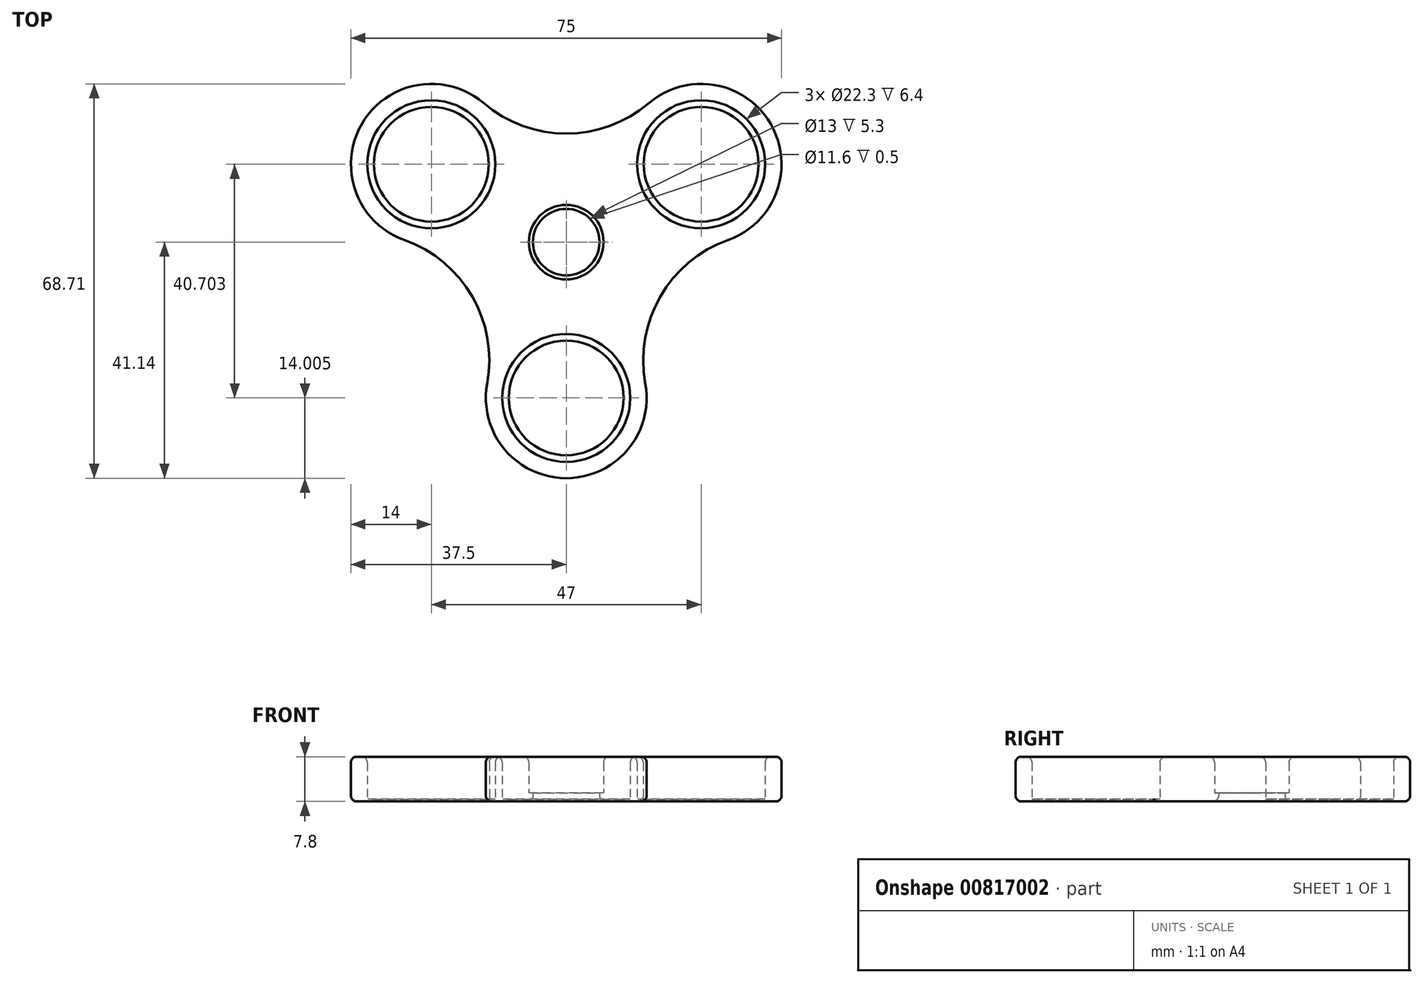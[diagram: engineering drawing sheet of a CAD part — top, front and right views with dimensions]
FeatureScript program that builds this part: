
annotation { "Feature Type Name" : "Feature", "Feature Type Description" : "" }
export const myFeature = defineFeature(function(context is Context, id is Id, definition is map)
    precondition{}
    {
        {
            var Q0;
            Q0=qCreatedBy(makeId("Top.planeOp"),FACE);
            var sketch = newSketch(context, id + "F0", { "sketchPlane" : qUnion([Q0])});
            skCircle(sketch, "E0.cCircle", {"center": v(0, 0) * mm, "radius": 13.57 * mm, "construction": true});
            skLineSegment(sketch, "E0.0", {"start": v(-23.5, 13.57) * mm, "end": v(23.5, 13.57) * mm, "construction": true});
            skLineSegment(sketch, "E0.1", {"start": v(23.5, 13.57) * mm, "end": v(0, -27.14) * mm, "construction": true});
            skLineSegment(sketch, "E0.2", {"start": v(0, -27.14) * mm, "end": v(-23.5, 13.57) * mm, "construction": true});
            skPoint(sketch, "E0.0.midPoint", {"position": v(0, 13.57) * mm});
            skCircle(sketch, "E1", {"center": v(-23.5, 13.57) * mm, "radius": 11.15 * mm});
            skCircle(sketch, "E2", {"center": v(-23.5, 13.57) * mm, "radius": 14 * mm});
            skCircle(sketch, "E3", {"center": v(0, -27.14) * mm, "radius": 11.15 * mm});
            skCircle(sketch, "E4", {"center": v(0, -27.14) * mm, "radius": 14 * mm});
            skCircle(sketch, "E5", {"center": v(23.5, 13.57) * mm, "radius": 14 * mm});
            skCircle(sketch, "E6", {"center": v(23.5, 13.57) * mm, "radius": 11.15 * mm});
            skCircle(sketch, "E7", {"center": v(0, 0) * mm, "radius": 41.14 * mm, "construction": true});
            skPoint(sketch, "E8", {"position": v(-11.75, -6.78) * mm});
            skPoint(sketch, "E9", {"position": v(11.75, -6.78) * mm});
            skLineSegment(sketch, "E10", {"start": v(0, 0) * mm, "end": v(-11.75, -6.78) * mm, "construction": true});
            skLineSegment(sketch, "E11", {"start": v(0, 0) * mm, "end": v(0, 13.57) * mm, "construction": true});
            skLineSegment(sketch, "E12", {"start": v(0, 0) * mm, "end": v(11.75, -6.78) * mm, "construction": true});
            skLineSegment(sketch, "E13", {"start": v(-11.75, -6.78) * mm, "end": v(-35.62, -20.57) * mm, "construction": true});
            skLineSegment(sketch, "E14", {"start": v(11.75, -6.78) * mm, "end": v(35.62, -20.57) * mm, "construction": true});
            skLineSegment(sketch, "E15", {"start": v(0, 13.57) * mm, "end": v(0, 41.14) * mm, "construction": true});
            skCircle(sketch, "E16", {"center": v(0, 41.14) * mm, "radius": 22.22 * mm});
            skCircle(sketch, "E17", {"center": v(-35.62, -20.57) * mm, "radius": 22.22 * mm});
            skCircle(sketch, "E18", {"center": v(35.62, -20.57) * mm, "radius": 22.22 * mm});
            skCircle(sketch, "E19", {"center": v(0, 0) * mm, "radius": 6.5 * mm});
            skSolve(sketch);
        }
        {
            var Q0;
            Q0=makeQuery(id+"F0.imprint","IMPRINT",FACE,{"disambiguationData":[TD([[makeQuery(id+"F0.imprint","IMPRINT",EDGE,{"derivedFrom":sQuery(id+"F0.wireOp",EDGE,"E19")}),-1.0]])]});
            var Q1;
            Q1=makeQuery(id+"F0.imprint","IMPRINT",FACE,{"disambiguationData":[TD([[makeQuery(id+"F0.imprint","IMPRINT",EDGE,{"derivedFrom":sQuery(id+"F0.wireOp",EDGE,"E1")}),-1.0]])]});
            var Q2;
            Q2=makeQuery(id+"F0.imprint","IMPRINT",FACE,{"disambiguationData":[TD([[makeQuery(id+"F0.imprint","IMPRINT",EDGE,{"derivedFrom":sQuery(id+"F0.wireOp",EDGE,"E6")}),-1.0]])]});
            var Q3;
            Q3=makeQuery(id+"F0.imprint","IMPRINT",FACE,{"disambiguationData":[TD([[makeQuery(id+"F0.imprint","IMPRINT",EDGE,{"derivedFrom":sQuery(id+"F0.wireOp",EDGE,"E3")}),-1.0]])]});
            extrude(context, id + "F1", {"entities" : qUnion([Q0, Q1, Q2, Q3]), "depth" : 7.8 * mm, "offsetDistance" : 25 * mm});
        }
        {
            var Q0;
            Q0=makeQuery(id+"F1.opExtrude","CAP_FACE",FACE,{"disambiguationData":[OSD([sQuery(id+"F0.wireOp",EDGE,"E1"),sQuery(id+"F0.wireOp",EDGE,"E2"),sQuery(id+"F0.wireOp",EDGE,"E3"),sQuery(id+"F0.wireOp",EDGE,"E4"),sQuery(id+"F0.wireOp",EDGE,"E5"),sQuery(id+"F0.wireOp",EDGE,"E6"),sQuery(id+"F0.wireOp",EDGE,"E16"),sQuery(id+"F0.wireOp",EDGE,"E17"),sQuery(id+"F0.wireOp",EDGE,"E18"),sQuery(id+"F0.wireOp",EDGE,"E19")])],"isStart":true});
            var sketch = newSketch(context, id + "F2", { "sketchPlane" : qUnion([Q0])});
            skCircle(sketch, "E20", {"center": v(0, 27.14) * mm, "radius": 10 * mm});
            skCircle(sketch, "E21", {"center": v(23.5, -13.57) * mm, "radius": 10 * mm});
            skCircle(sketch, "E22", {"center": v(-23.5, -13.57) * mm, "radius": 10 * mm});
            skCircle(sketch, "E23", {"center": v(0, 27.14) * mm, "radius": 11.15 * mm});
            skCircle(sketch, "E24", {"center": v(23.5, -13.57) * mm, "radius": 11.15 * mm});
            skCircle(sketch, "E25", {"center": v(-23.5, -13.57) * mm, "radius": 11.15 * mm});
            skSolve(sketch);
        }
        {
            var Q0;
            Q0 = qSketchRegion(id + "F2", true);
            extrude(context, id + "F3", {"entities" : qUnion([Q0]), "operationType" : NewBodyOperationType.ADD, "oppositeDirection" : true, "depth" : 0.4 * mm, "offsetDistance" : 25 * mm});
        }
        {
            var Q0;
            Q0=makeQuery(id+"F3.boolean.opBoolean","MERGE",FACE,{"derivedFrom":[makeQuery(id+"F1.opExtrude","CAP_FACE",FACE,{"disambiguationData":[OSD([sQuery(id+"F0.wireOp",EDGE,"E1"),sQuery(id+"F0.wireOp",EDGE,"E2"),sQuery(id+"F0.wireOp",EDGE,"E3"),sQuery(id+"F0.wireOp",EDGE,"E4"),sQuery(id+"F0.wireOp",EDGE,"E5"),sQuery(id+"F0.wireOp",EDGE,"E6"),sQuery(id+"F0.wireOp",EDGE,"E16"),sQuery(id+"F0.wireOp",EDGE,"E17"),sQuery(id+"F0.wireOp",EDGE,"E18"),sQuery(id+"F0.wireOp",EDGE,"E19")])],"isStart":true}),makeQuery(id+"F3.opExtrude","CAP_FACE",FACE,{"disambiguationData":[OSD([sQuery(id+"F2.wireOp",EDGE,"E20"),sQuery(id+"F2.wireOp",EDGE,"E23")])],"isStart":true}),makeQuery(id+"F3.opExtrude","CAP_FACE",FACE,{"disambiguationData":[OSD([sQuery(id+"F2.wireOp",EDGE,"E21"),sQuery(id+"F2.wireOp",EDGE,"E24")])],"isStart":true}),makeQuery(id+"F3.opExtrude","CAP_FACE",FACE,{"disambiguationData":[OSD([sQuery(id+"F2.wireOp",EDGE,"E22"),sQuery(id+"F2.wireOp",EDGE,"E25")])],"isStart":true})]});
            var sketch = newSketch(context, id + "F4", { "sketchPlane" : qUnion([Q0])});
            skCircle(sketch, "E26", {"center": v(0, 0) * mm, "radius": 5.8 * mm});
            skCircle(sketch, "E27", {"center": v(0, 0) * mm, "radius": 6.5 * mm});
            skSolve(sketch);
        }
        {
            var Q0;
            Q0 = qSketchRegion(id + "F4", true);
            extrude(context, id + "F5", {"entities" : qUnion([Q0]), "operationType" : NewBodyOperationType.ADD, "oppositeDirection" : true, "depth" : 1.5 * mm, "offsetDistance" : 25 * mm});
        }
        {
            var Q0;
            Q0=makeQuery(id+"F1.opExtrude","CAP_EDGE",EDGE,{"disambiguationData":[OSD([sQuery(id+"F0.wireOp",EDGE,"E1")])],"isStart":false});
            var Q1;
            Q1=makeQuery(id+"F1.opExtrude","CAP_EDGE",EDGE,{"disambiguationData":[OSD([sQuery(id+"F0.wireOp",EDGE,"E3")])],"isStart":false});
            var Q2;
            Q2=makeQuery(id+"F1.opExtrude","CAP_EDGE",EDGE,{"disambiguationData":[OSD([sQuery(id+"F0.wireOp",EDGE,"E19")])],"isStart":false});
            var Q3;
            Q3=makeQuery(id+"F1.opExtrude","CAP_EDGE",EDGE,{"disambiguationData":[OSD([sQuery(id+"F0.wireOp",EDGE,"E6")])],"isStart":false});
            var Q4;
            Q4=makeQuery(id+"F1.opExtrude","CAP_FACE",FACE,{"disambiguationData":[OSD([sQuery(id+"F0.wireOp",EDGE,"E1"),sQuery(id+"F0.wireOp",EDGE,"E2"),sQuery(id+"F0.wireOp",EDGE,"E3"),sQuery(id+"F0.wireOp",EDGE,"E4"),sQuery(id+"F0.wireOp",EDGE,"E5"),sQuery(id+"F0.wireOp",EDGE,"E6"),sQuery(id+"F0.wireOp",EDGE,"E16"),sQuery(id+"F0.wireOp",EDGE,"E17"),sQuery(id+"F0.wireOp",EDGE,"E18"),sQuery(id+"F0.wireOp",EDGE,"E19")])],"isStart":false});
            var Q5;
            Q5=makeQuery(id+"F5.boolean.opBoolean","MERGE",FACE,{"derivedFrom":[makeQuery(id+"F3.boolean.opBoolean","MERGE",FACE,{"derivedFrom":[makeQuery(id+"F1.opExtrude","CAP_FACE",FACE,{"disambiguationData":[OSD([sQuery(id+"F0.wireOp",EDGE,"E1"),sQuery(id+"F0.wireOp",EDGE,"E2"),sQuery(id+"F0.wireOp",EDGE,"E3"),sQuery(id+"F0.wireOp",EDGE,"E4"),sQuery(id+"F0.wireOp",EDGE,"E5"),sQuery(id+"F0.wireOp",EDGE,"E6"),sQuery(id+"F0.wireOp",EDGE,"E16"),sQuery(id+"F0.wireOp",EDGE,"E17"),sQuery(id+"F0.wireOp",EDGE,"E18"),sQuery(id+"F0.wireOp",EDGE,"E19")])],"isStart":true}),makeQuery(id+"F3.opExtrude","CAP_FACE",FACE,{"disambiguationData":[OSD([sQuery(id+"F2.wireOp",EDGE,"E20"),sQuery(id+"F2.wireOp",EDGE,"E23")])],"isStart":true}),makeQuery(id+"F3.opExtrude","CAP_FACE",FACE,{"disambiguationData":[OSD([sQuery(id+"F2.wireOp",EDGE,"E21"),sQuery(id+"F2.wireOp",EDGE,"E24")])],"isStart":true}),makeQuery(id+"F3.opExtrude","CAP_FACE",FACE,{"disambiguationData":[OSD([sQuery(id+"F2.wireOp",EDGE,"E22"),sQuery(id+"F2.wireOp",EDGE,"E25")])],"isStart":true})]}),makeQuery(id+"F5.opExtrude","CAP_FACE",FACE,{"disambiguationData":[OSD([sQuery(id+"F4.wireOp",EDGE,"E26"),sQuery(id+"F4.wireOp",EDGE,"E27")])],"isStart":true})]});
            fillet(context, id + "F6", {"entities" : qUnion([Q0, Q1, Q2, Q3, Q4, Q5]), "radius" : 1 * mm, "tangentPropagation" : true, "allowEdgeOverflow" : false});
        }
    });
